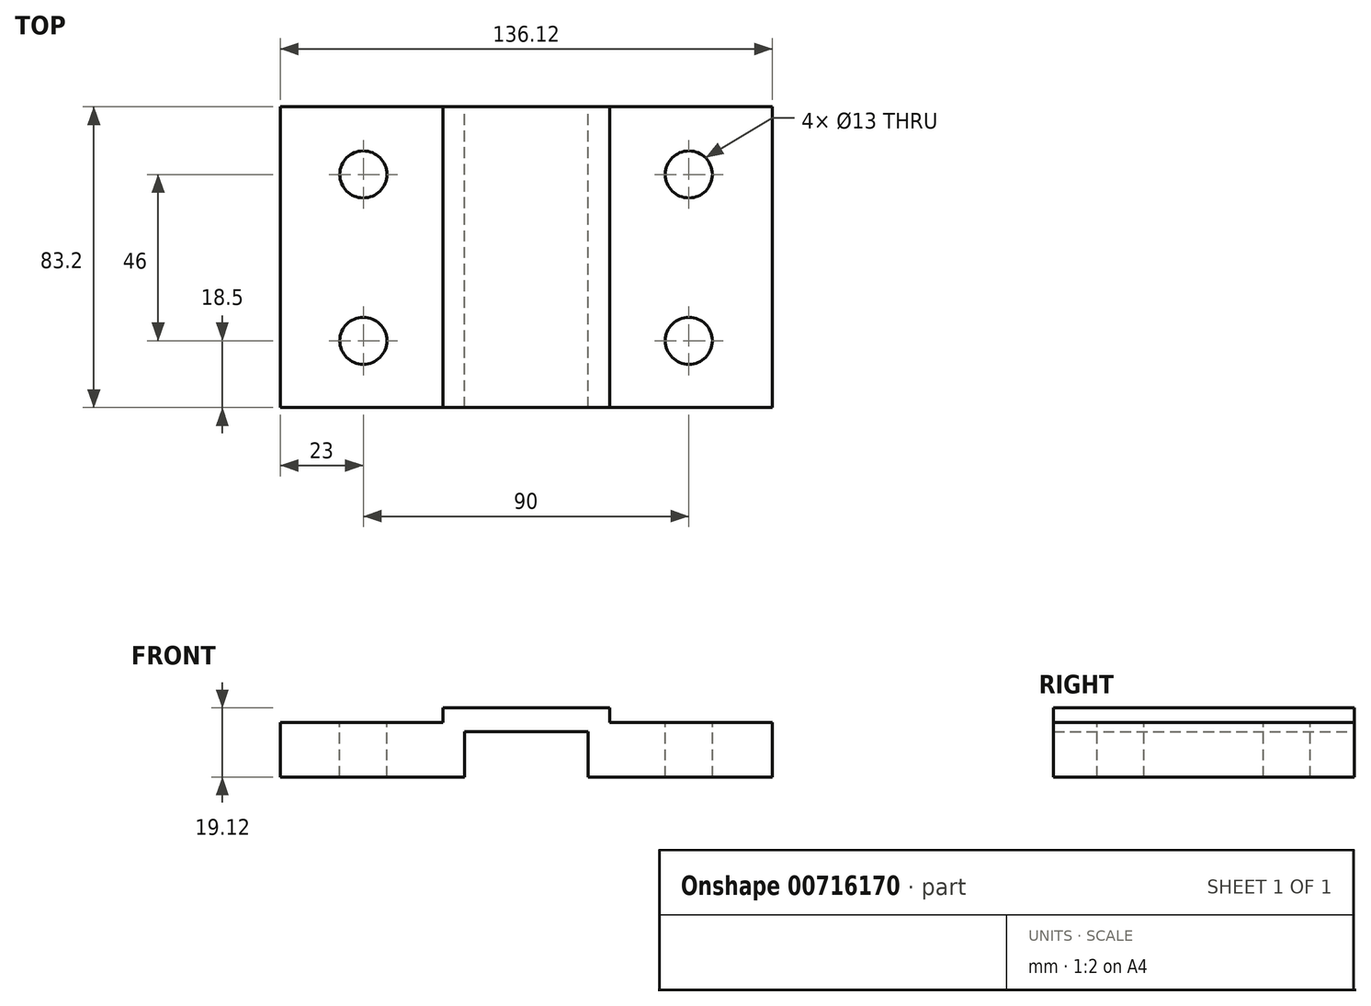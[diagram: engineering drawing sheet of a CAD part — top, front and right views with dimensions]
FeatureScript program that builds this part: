
annotation { "Feature Type Name" : "Feature", "Feature Type Description" : "" }
export const myFeature = defineFeature(function(context is Context, id is Id, definition is map)
    precondition{}
    {
        {
            var Q0;
            Q0=qCreatedBy(makeId("Front.planeOp"),FACE);
            var sketch = newSketch(context, id + "F0", { "sketchPlane" : qUnion([Q0])});
            skLineSegment(sketch, "E0", {"start": v(-51, -12.5) * mm, "end": v(0, -12.5) * mm});
            skLineSegment(sketch, "E1", {"start": v(0, -12.5) * mm, "end": v(0, 0) * mm});
            skLineSegment(sketch, "E2", {"start": v(0, 0) * mm, "end": v(34.12, 0) * mm});
            skLineSegment(sketch, "E3", {"start": v(34.12, 0) * mm, "end": v(34.12, -12.5) * mm});
            skLineSegment(sketch, "E4", {"start": v(34.12, -12.5) * mm, "end": v(85.12, -12.5) * mm});
            skLineSegment(sketch, "E5", {"start": v(40.12, 2.58) * mm, "end": v(40.12, 6.62) * mm});
            skLineSegment(sketch, "E6", {"start": v(40.12, 6.62) * mm, "end": v(-6, 6.62) * mm});
            skLineSegment(sketch, "E7", {"start": v(-6, 6.62) * mm, "end": v(-6, 2.58) * mm});
            skLineSegment(sketch, "E8", {"start": v(-51, -12.5) * mm, "end": v(-51, 2.58) * mm});
            skLineSegment(sketch, "E9", {"start": v(85.12, -12.5) * mm, "end": v(85.12, 2.58) * mm});
            skLineSegment(sketch, "E10", {"start": v(-51, 2.58) * mm, "end": v(-6, 2.58) * mm});
            skLineSegment(sketch, "E11", {"start": v(40.12, 2.58) * mm, "end": v(85.12, 2.58) * mm});
            skSolve(sketch);
        }
        {
            var Q0;
            Q0=makeQuery(id+"F0.imprint","IMPRINT",FACE,{"disambiguationData":[TD([[makeQuery(id+"F0.imprint","IMPRINT",EDGE,{"derivedFrom":sQuery(id+"F0.wireOp",EDGE,"E0")}),1.0]])]});
            extrude(context, id + "F1", {"entities" : qUnion([Q0]), "endBound" : BoundingType.SYMMETRIC, "depth" : 83.2 * mm, "offsetDistance" : 25 * mm});
        }
        {
            var Q0;
            Q0=makeQuery(id+"F1.opExtrude","SWEPT_FACE",FACE,{"disambiguationData":[OSD([sQuery(id+"F0.wireOp",EDGE,"E10")])]});
            var sketch = newSketch(context, id + "F2", { "sketchPlane" : qUnion([Q0])});
            skPoint(sketch, "E12", {"position": v(-28, -23.1) * mm});
            skPoint(sketch, "E13.0.1.0", {"position": v(-28, 22.9) * mm});
            skPoint(sketch, "E13.1.0.0", {"position": v(62, -23.1) * mm});
            skPoint(sketch, "E13.1.1.0", {"position": v(62, 22.9) * mm});
            skLineSegment(sketch, "E13.direction1", {"start": v(-28, -23.1) * mm, "end": v(62, -23.1) * mm, "construction": true});
            skLineSegment(sketch, "E13.direction2", {"start": v(-28, 22.9) * mm, "end": v(-28, -23.1) * mm, "construction": true});
            skSolve(sketch);
        }
        {
            var Q0;
            Q0=sQuery(id+"F2.wireOp",VERTEX,"E12");
            var Q1;
            Q1=sQuery(id+"F2.wireOp",VERTEX,"E13.0.1.0");
            var Q2;
            Q2=sQuery(id+"F2.wireOp",VERTEX,"E13.1.1.0");
            var Q3;
            Q3=sQuery(id+"F2.wireOp",VERTEX,"E13.1.0.0");
            var Q4;
            Q4=makeQuery(id+"F1.opExtrude","SWEPT_BODY",BODY,{"disambiguationData":[OSD([sQuery(id+"F0.wireOp",EDGE,"E0"),sQuery(id+"F0.wireOp",EDGE,"E1"),sQuery(id+"F0.wireOp",EDGE,"E2"),sQuery(id+"F0.wireOp",EDGE,"E3"),sQuery(id+"F0.wireOp",EDGE,"E4"),sQuery(id+"F0.wireOp",EDGE,"E5"),sQuery(id+"F0.wireOp",EDGE,"E6"),sQuery(id+"F0.wireOp",EDGE,"E7"),sQuery(id+"F0.wireOp",EDGE,"E8"),sQuery(id+"F0.wireOp",EDGE,"E9"),sQuery(id+"F0.wireOp",EDGE,"E10"),sQuery(id+"F0.wireOp",EDGE,"E11")])]});
            hole(context, id + "F3", {"style" : HoleStyle.SIMPLE, "endStyle" : HoleEndStyle.THROUGH, "holeDiameter" : 13 * mm, "majorDiameter" : 5 * mm, "isTappedThrough" : true, "tappedDepth" : 12 * mm, "tapClearance" : 0, "locations" : qUnion([Q0, Q1, Q2, Q3]), "scope" : qUnion([Q4])});
        }
    });
